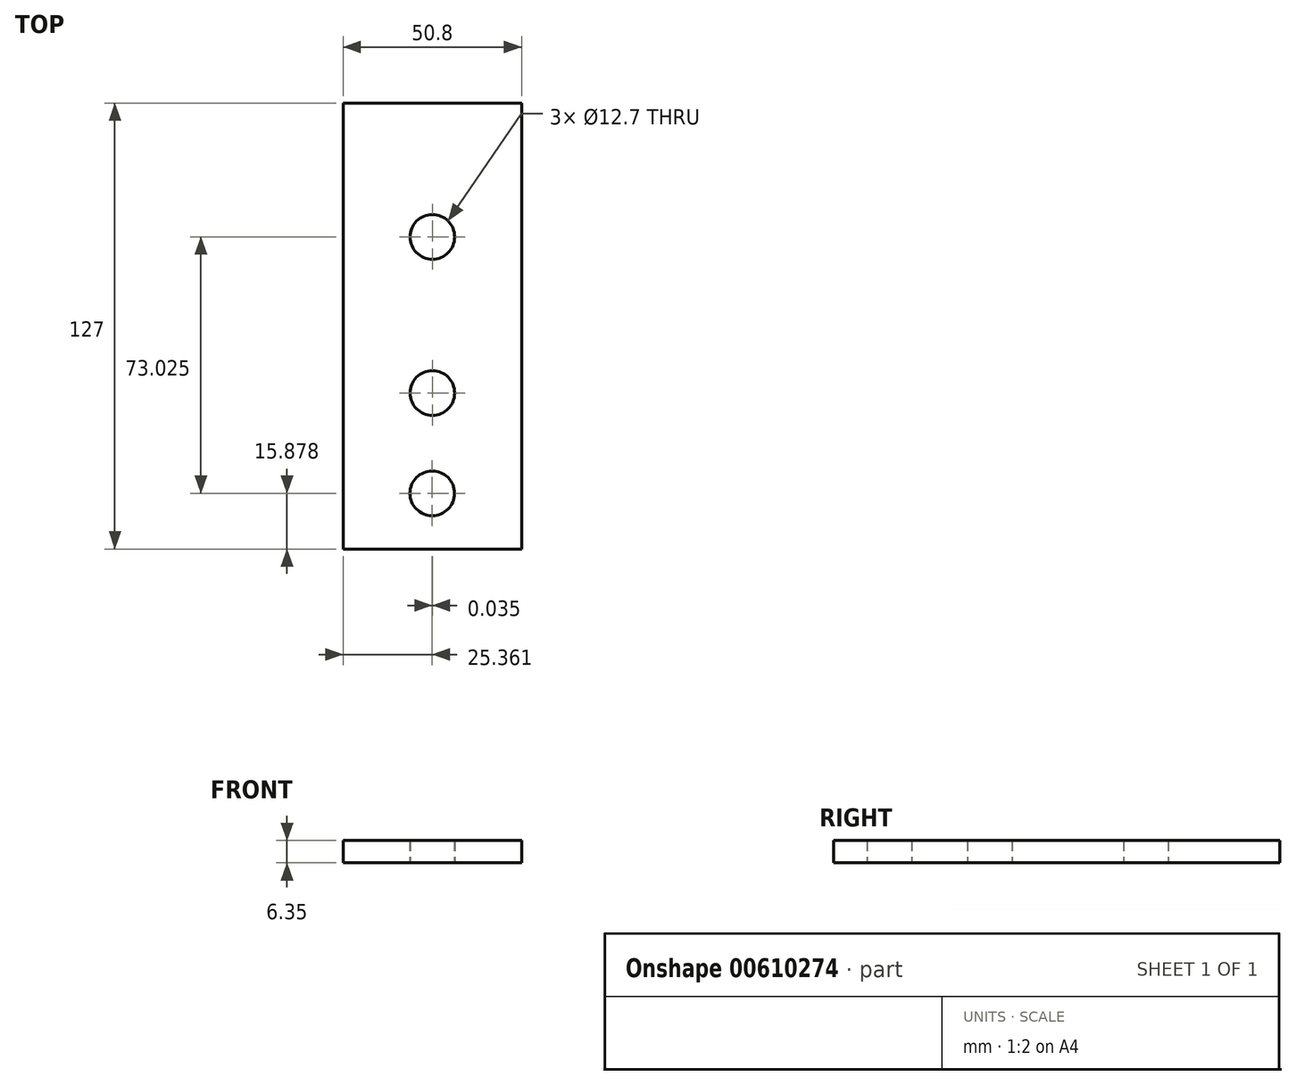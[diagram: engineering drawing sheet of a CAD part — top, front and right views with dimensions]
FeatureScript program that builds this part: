
annotation { "Feature Type Name" : "Feature", "Feature Type Description" : "" }
export const myFeature = defineFeature(function(context is Context, id is Id, definition is map)
    precondition{}
    {
        {
            var Q0;
            Q0=qCreatedBy(makeId("Top.planeOp"),FACE);
            var sketch = newSketch(context, id + "F0", { "sketchPlane" : qUnion([Q0])});
            skLineSegment(sketch, "E0.bottom", {"start": v(-30.48, 94.55) * mm, "end": v(20.32, 94.55) * mm});
            skLineSegment(sketch, "E0.top", {"start": v(-30.48, -32.45) * mm, "end": v(20.32, -32.45) * mm});
            skLineSegment(sketch, "E0.left", {"start": v(-30.48, 94.55) * mm, "end": v(-30.48, -32.45) * mm});
            skLineSegment(sketch, "E0.right", {"start": v(20.32, 94.55) * mm, "end": v(20.32, -32.45) * mm});
            skCircle(sketch, "E1", {"center": v(-5.08, 56.45) * mm, "radius": 6.35 * mm});
            skCircle(sketch, "E2", {"center": v(-5.08, 12) * mm, "radius": 6.35 * mm});
            skCircle(sketch, "E3", {"center": v(-5.12, -16.57) * mm, "radius": 6.35 * mm});
            skSolve(sketch);
        }
        {
            var Q0;
            Q0=makeQuery(id+"F0.imprint","IMPRINT",FACE,{"disambiguationData":[TD([[makeQuery(id+"F0.imprint","IMPRINT",EDGE,{"derivedFrom":sQuery(id+"F0.wireOp",EDGE,"E0.bottom")}),-1.0]])]});
            extrude(context, id + "F1", {"entities" : qUnion([Q0]), "depth" : 6.35 * mm, "offsetDistance" : 25.4 * mm});
        }
    });
